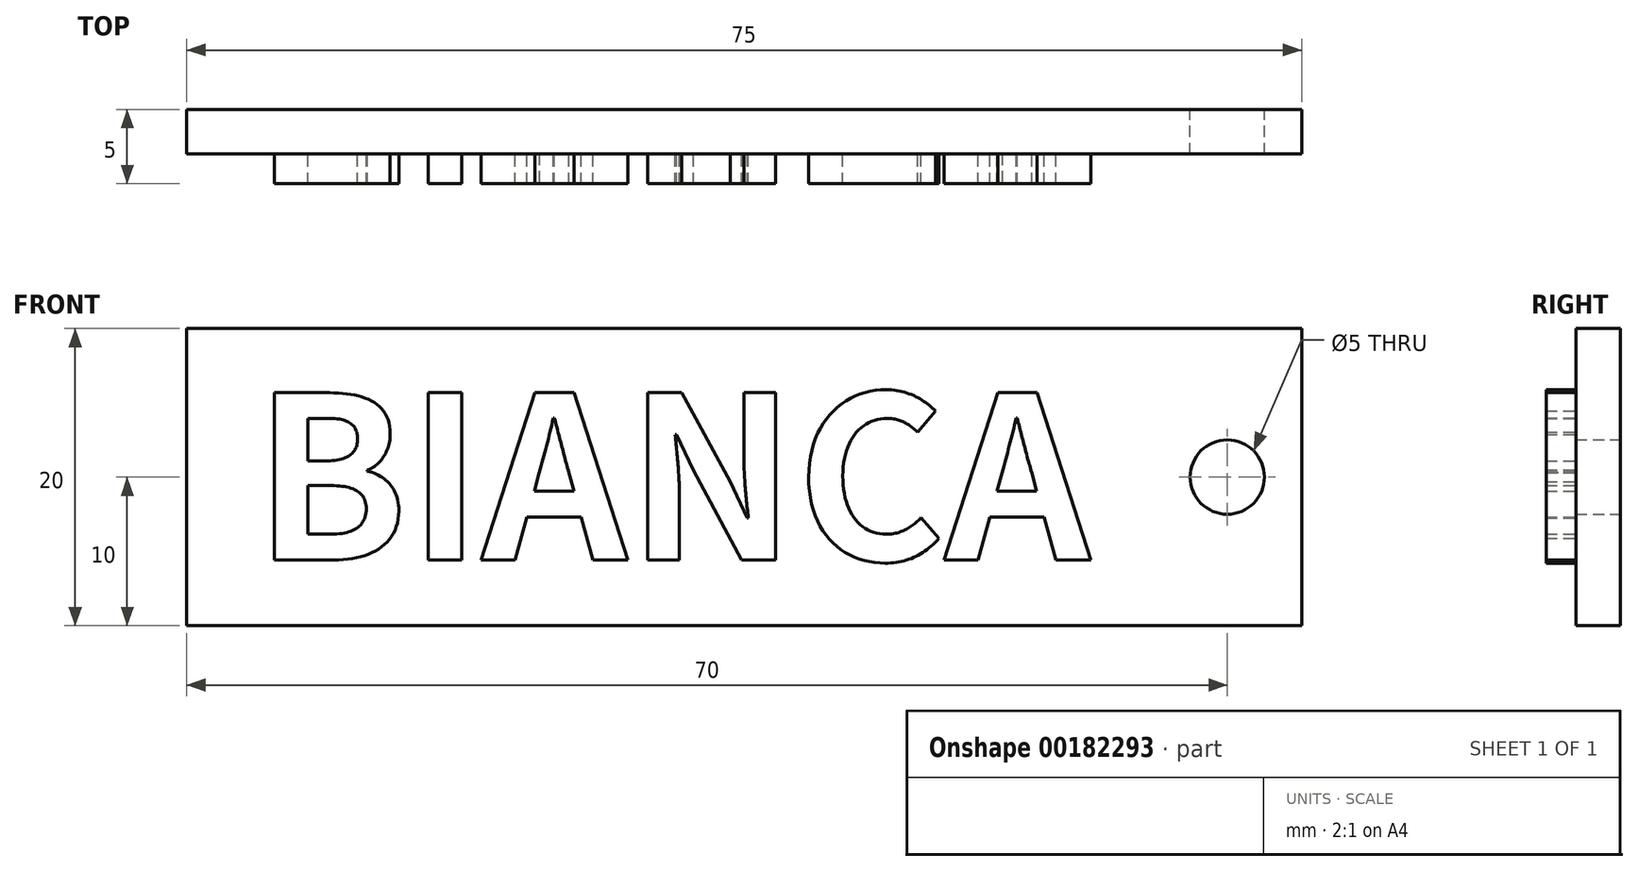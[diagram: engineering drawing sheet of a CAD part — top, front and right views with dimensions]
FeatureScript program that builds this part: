
annotation { "Feature Type Name" : "Feature", "Feature Type Description" : "" }
export const myFeature = defineFeature(function(context is Context, id is Id, definition is map)
    precondition{}
    {
        {
            var Q0;
            Q0=qCreatedBy(makeId("Front.planeOp"),FACE);
            var sketch = newSketch(context, id + "F0", { "sketchPlane" : qUnion([Q0])});
            skLineSegment(sketch, "E0.bottom", {"start": v(0, 0) * mm, "end": v(75, 0) * mm});
            skLineSegment(sketch, "E0.top", {"start": v(0, -20) * mm, "end": v(75, -20) * mm});
            skLineSegment(sketch, "E0.left", {"start": v(0, 0) * mm, "end": v(0, -20) * mm});
            skLineSegment(sketch, "E0.right", {"start": v(75, 0) * mm, "end": v(75, -20) * mm});
            skCircle(sketch, "E1", {"center": v(70, -10) * mm, "radius": 2.5 * mm});
            skPoint(sketch, "E1.centerSnap0", {"position": v(75, -10) * mm});
            skSolve(sketch);
        }
        {
            var Q0;
            Q0=makeQuery(id+"F0.imprint","IMPRINT",FACE,{"disambiguationData":[TD([[makeQuery(id+"F0.imprint","IMPRINT",EDGE,{"derivedFrom":sQuery(id+"F0.wireOp",EDGE,"E0.bottom")}),-1.0]])]});
            extrude(context, id + "F1", {"entities" : qUnion([Q0]), "depth" : 3 * mm});
        }
        {
            var Q0;
            Q0=makeQuery(id+"F1.opExtrude","CAP_FACE",FACE,{"disambiguationData":[OSD([sQuery(id+"F0.wireOp",EDGE,"E0.bottom"),sQuery(id+"F0.wireOp",EDGE,"E0.top"),sQuery(id+"F0.wireOp",EDGE,"E0.left"),sQuery(id+"F0.wireOp",EDGE,"E0.right"),sQuery(id+"F0.wireOp",EDGE,"E1")])],"isStart":false});
            var sketch = newSketch(context, id + "F2", { "sketchPlane" : qUnion([Q0])});
            skText(sketch, "E2", { "text": "BIANCA", "fontName": "NotoSansCJKtc-Bold.otf"});
            const initialGuessF2  = {"E2": [0.0045, -0.01558, 1, 0, 0.01095]};
            skSetInitialGuess(sketch, initialGuessF2);
            skSolve(sketch);
        }
        {
            var Q0;
            Q0 = qSketchRegion(id + "F2", true);
            extrude(context, id + "F3", {"entities" : qUnion([Q0]), "operationType" : NewBodyOperationType.ADD, "depth" : 2 * mm});
        }
    });
